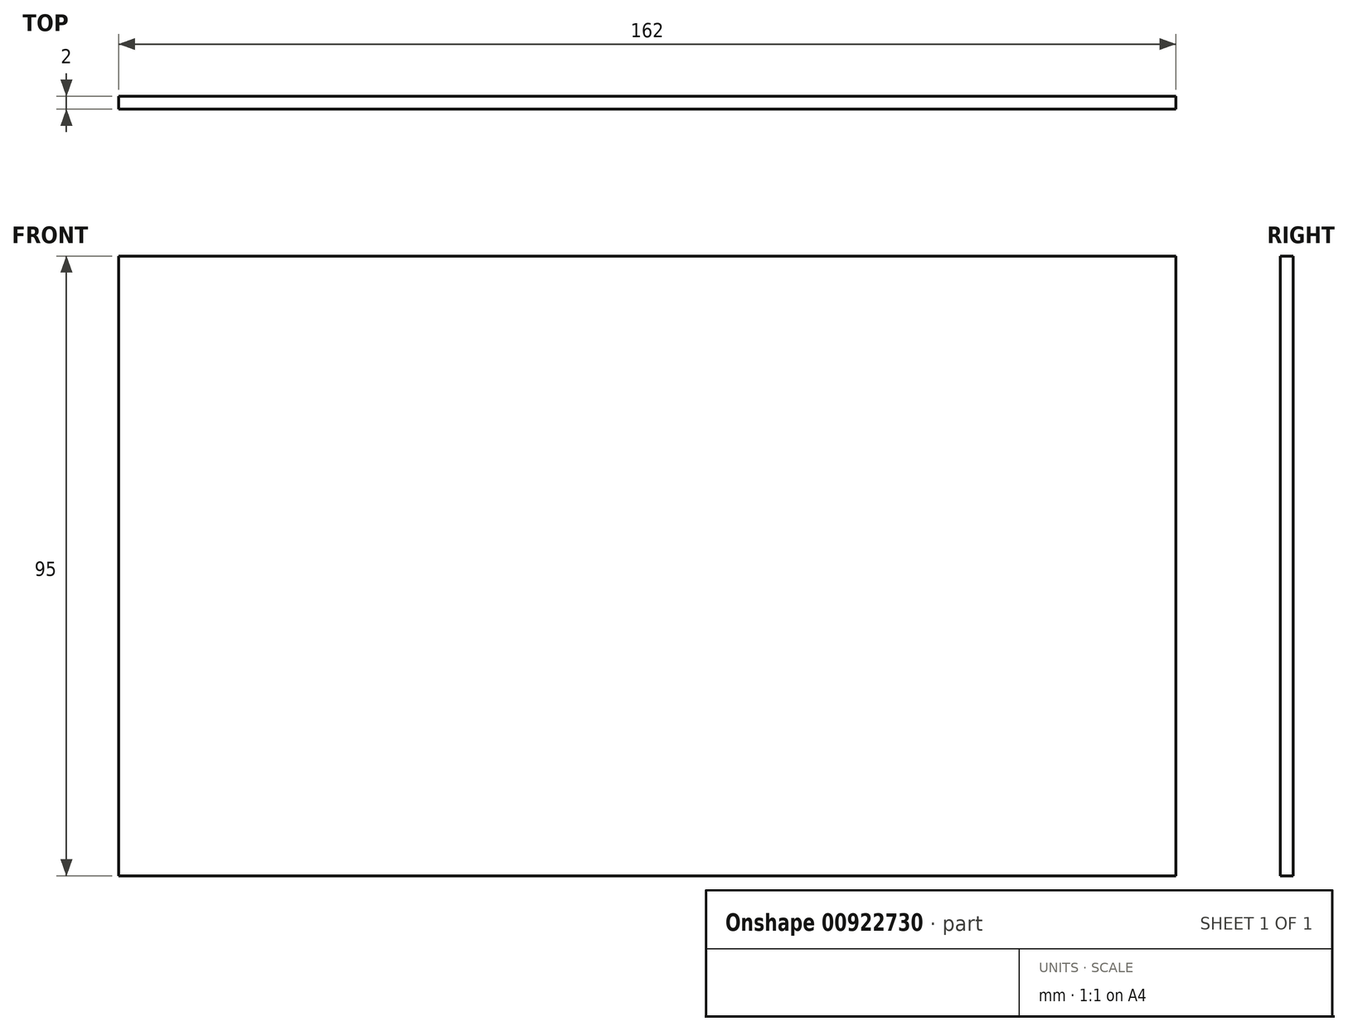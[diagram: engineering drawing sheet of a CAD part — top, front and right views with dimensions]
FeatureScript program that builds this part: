
annotation { "Feature Type Name" : "Feature", "Feature Type Description" : "" }
export const myFeature = defineFeature(function(context is Context, id is Id, definition is map)
    precondition{}
    {
        {
            var Q0;
            Q0=qCreatedBy(makeId("Front.planeOp"),FACE);
            var sketch = newSketch(context, id + "F0", { "sketchPlane" : qUnion([Q0])});
            skLineSegment(sketch, "E0.bottom", {"start": v(81, -47.5) * mm, "end": v(-81, -47.5) * mm});
            skLineSegment(sketch, "E0.top", {"start": v(81, 47.5) * mm, "end": v(-81, 47.5) * mm});
            skLineSegment(sketch, "E0.left", {"start": v(81, -47.5) * mm, "end": v(81, 47.5) * mm});
            skLineSegment(sketch, "E0.right", {"start": v(-81, -47.5) * mm, "end": v(-81, 47.5) * mm});
            skPoint(sketch, "E0.middle", {"position": v(0, 0) * mm});
            skSolve(sketch);
        }
        {
            var Q0;
            Q0 = qSketchRegion(id + "F0", true);
            extrude(context, id + "F1", {"entities" : qUnion([Q0]), "endBound" : BoundingType.SYMMETRIC, "depth" : 2 * mm, "offsetDistance" : 25 * mm});
        }
    });
